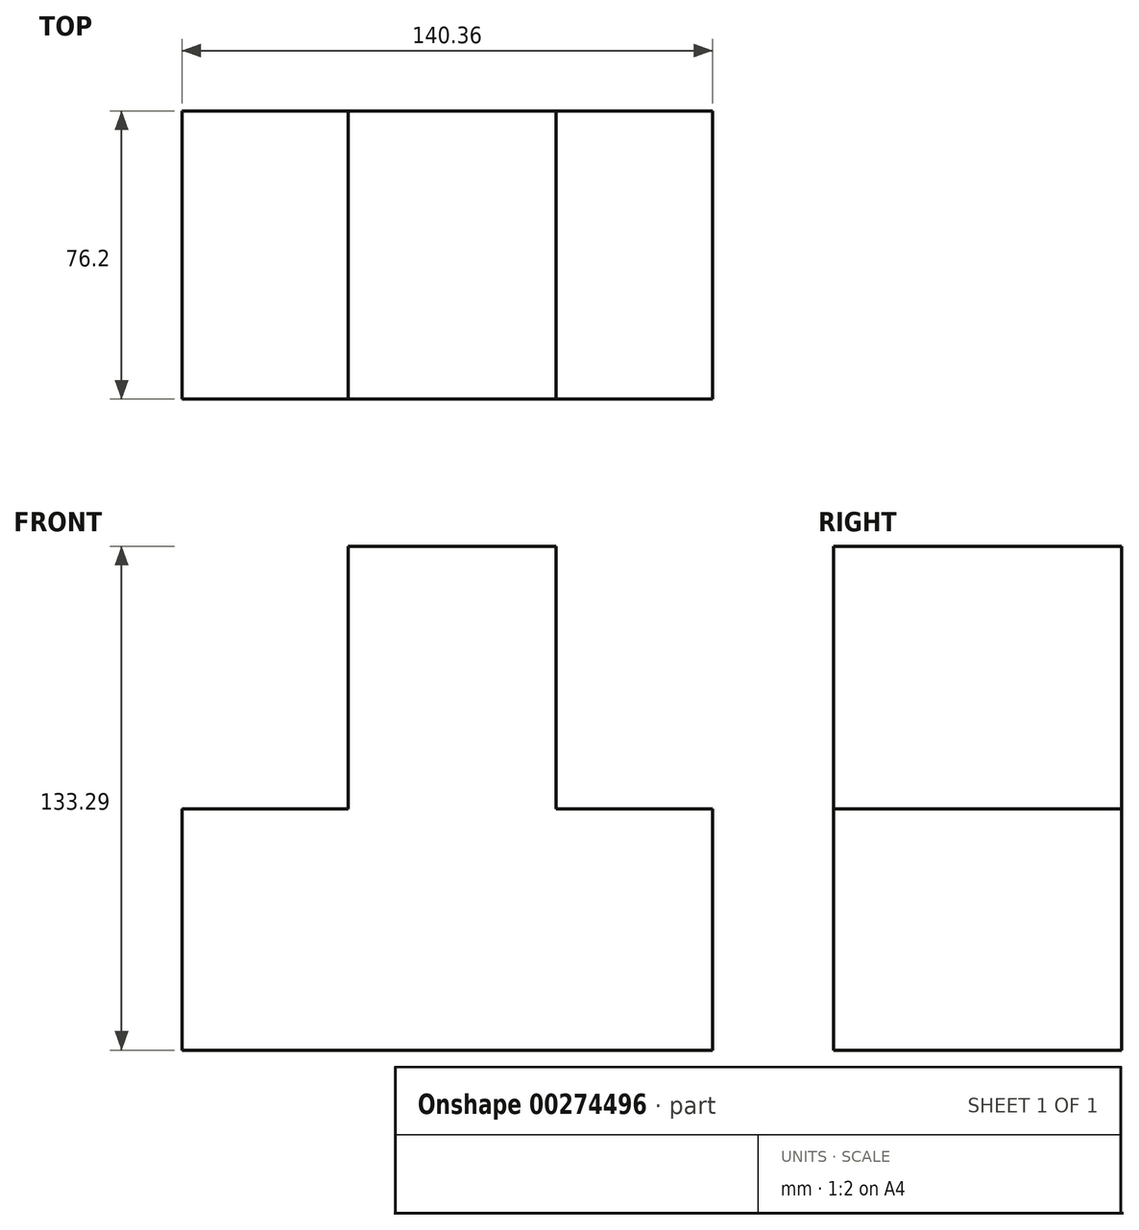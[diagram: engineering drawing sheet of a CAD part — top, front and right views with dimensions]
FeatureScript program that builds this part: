
annotation { "Feature Type Name" : "Feature", "Feature Type Description" : "" }
export const myFeature = defineFeature(function(context is Context, id is Id, definition is map)
    precondition{}
    {
        {
            var Q0;
            Q0=qCreatedBy(makeId("Front.planeOp"),FACE);
            var sketch = newSketch(context, id + "F0", { "sketchPlane" : qUnion([Q0])});
            skLineSegment(sketch, "E0", {"start": v(73.14, 0) * mm, "end": v(31.7, 0) * mm});
            skLineSegment(sketch, "E1", {"start": v(31.7, 0) * mm, "end": v(31.7, 69.5) * mm});
            skLineSegment(sketch, "E2", {"start": v(31.7, 69.5) * mm, "end": v(-23.3, 69.5) * mm});
            skLineSegment(sketch, "E3", {"start": v(-23.3, 69.5) * mm, "end": v(-23.3, 0) * mm});
            skLineSegment(sketch, "E4", {"start": v(-23.3, 0) * mm, "end": v(-67.22, 0) * mm});
            skLineSegment(sketch, "E5", {"start": v(-67.22, 0) * mm, "end": v(-67.22, -63.78) * mm});
            skLineSegment(sketch, "E6", {"start": v(-67.22, -63.78) * mm, "end": v(64.73, -63.78) * mm});
            skLineSegment(sketch, "E7", {"start": v(64.73, -63.78) * mm, "end": v(73.14, -63.78) * mm});
            skLineSegment(sketch, "E8", {"start": v(73.14, -63.78) * mm, "end": v(73.14, 0) * mm});
            skSolve(sketch);
        }
        {
            var Q0;
            Q0=makeQuery(id+"F0.imprint","IMPRINT",FACE,{"disambiguationData":[TD([[makeQuery(id+"F0.imprint","IMPRINT",EDGE,{"derivedFrom":sQuery(id+"F0.wireOp",EDGE,"E0")}),1.0]])]});
            extrude(context, id + "F1", {"entities" : qUnion([Q0]), "depth" : 76.2 * mm});
        }
    });
